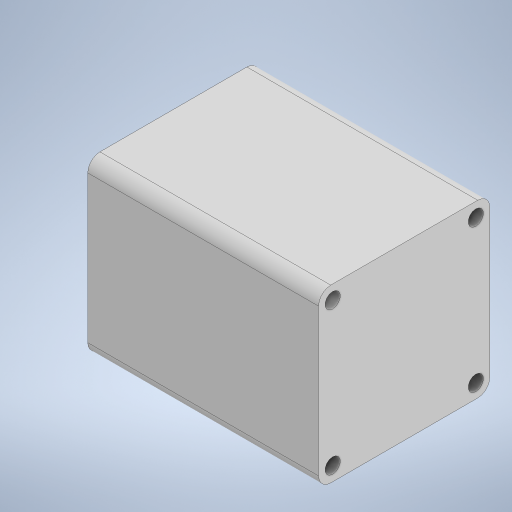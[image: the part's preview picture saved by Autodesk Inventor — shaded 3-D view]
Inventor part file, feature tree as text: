
AUTODESK INVENTOR PART (.ipt)
format: ipt  version: 2023 (Build 270158000, 158)  size: 221,184 bytes
history: native  units: mm
features: extrude x3, sketch x3
ambient origin geometry x8: Origin, YZ Plane, XZ Plane, XY Plane, X Axis, Y Axis, Z Axis, Center Point
bodies: Solid1 (feature_tree)
feature tree (6):
  extrude  "Extrusion1"  Depth=56.4mm
  extrude  "Extrusion2"  Depth=4.0mm
  extrude  "Extrusion3"  Depth=4.0mm
  sketch  "Sketch1"  dims[d0=56.4mm d1=47.14mm]
  sketch  "Sketch2"  dims[d2=5.0mm d3=4.0mm]
  sketch  "Sketch3"  dims[d4=4.0mm d5=4.0mm d6=4.0mm d7=76.0mm d8=0.0mm d9=38.1mm d10=1.6mm d11=0.0mm d12=8.0mm d13=20.0mm d14=0.0mm d15=0.5mm d16=0.872665mm d17=0.5mm d18=0.872665mm]
